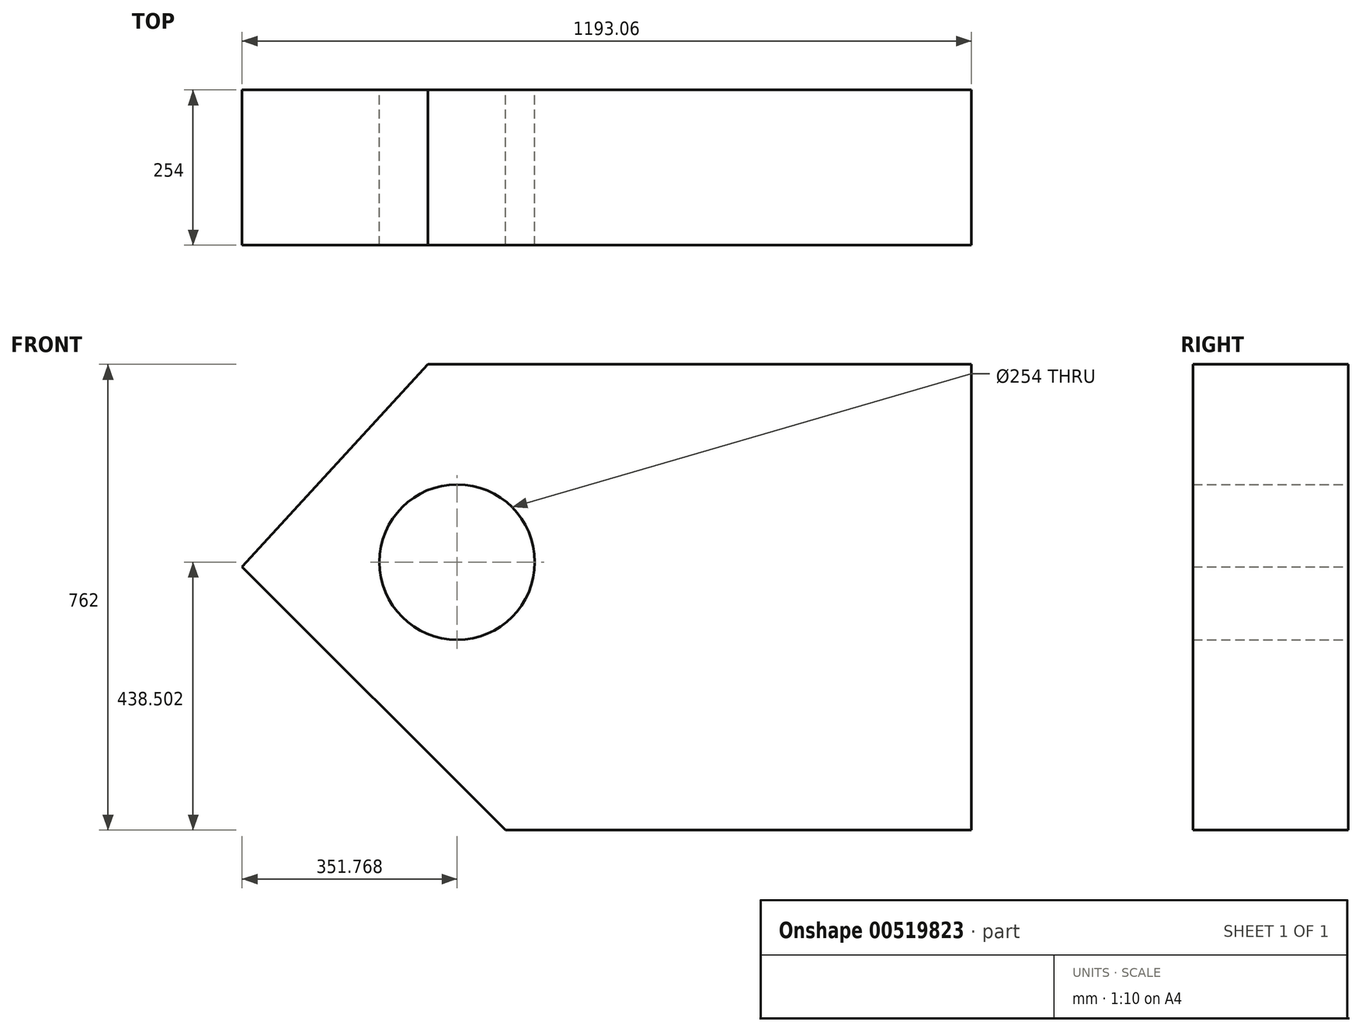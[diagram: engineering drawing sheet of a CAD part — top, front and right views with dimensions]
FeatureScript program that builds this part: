
annotation { "Feature Type Name" : "Feature", "Feature Type Description" : "" }
export const myFeature = defineFeature(function(context is Context, id is Id, definition is map)
    precondition{}
    {
        {
            var Q0;
            Q0=qCreatedBy(makeId("Front.planeOp"),FACE);
            var sketch = newSketch(context, id + "F0", { "sketchPlane" : qUnion([Q0])});
            skLineSegment(sketch, "E0", {"start": v(116.1, -263.74) * mm, "end": v(1005.1, -263.74) * mm});
            skLineSegment(sketch, "E1", {"start": v(1005.1, -263.74) * mm, "end": v(1005.1, -1025.74) * mm});
            skLineSegment(sketch, "E2", {"start": v(1005.1, -1025.74) * mm, "end": v(243.1, -1025.74) * mm});
            skLineSegment(sketch, "E3", {"start": v(243.1, -1025.74) * mm, "end": v(-187.96, -594.68) * mm});
            skLineSegment(sketch, "E4", {"start": v(116.1, -263.74) * mm, "end": v(-187.96, -594.68) * mm});
            skCircle(sketch, "E5", {"center": v(163.8, -587.24) * mm, "radius": 127 * mm});
            skSolve(sketch);
        }
        {
            var Q0;
            Q0=makeQuery(id+"F0.imprint","IMPRINT",FACE,{"disambiguationData":[TD([[makeQuery(id+"F0.imprint","IMPRINT",EDGE,{"derivedFrom":sQuery(id+"F0.wireOp",EDGE,"E0")}),-1.0]])]});
            extrude(context, id + "F1", {"entities" : qUnion([Q0]), "depth" : 254 * mm, "offsetDistance" : 25.4 * mm});
        }
    });
